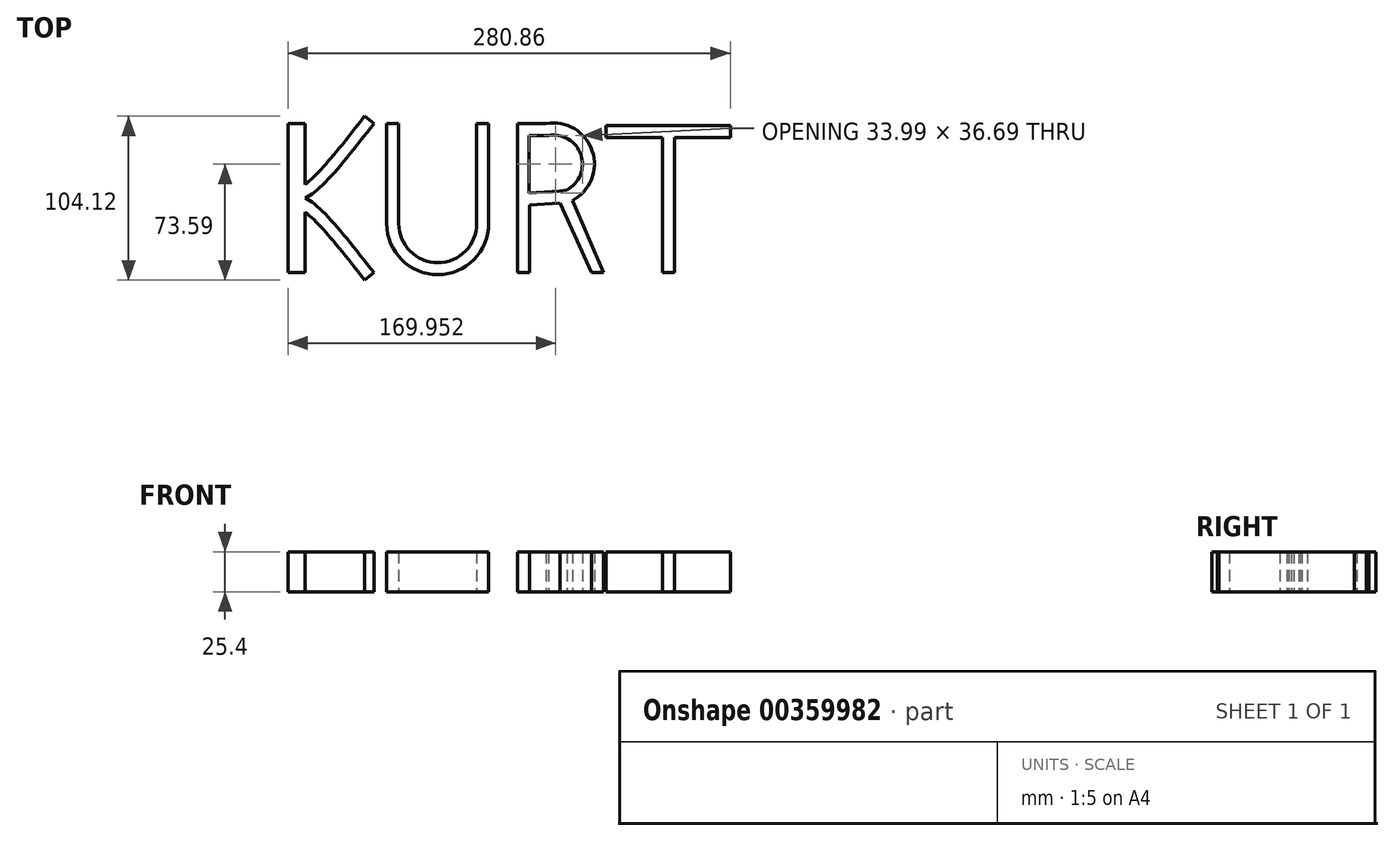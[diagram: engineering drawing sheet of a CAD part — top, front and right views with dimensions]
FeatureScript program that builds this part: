
annotation { "Feature Type Name" : "Feature", "Feature Type Description" : "" }
export const myFeature = defineFeature(function(context is Context, id is Id, definition is map)
    precondition{}
    {
        {
            var Q0;
            Q0=qCreatedBy(makeId("Top.planeOp"),FACE);
            var sketch = newSketch(context, id + "F0", { "sketchPlane" : qUnion([Q0])});
            skLineSegment(sketch, "E0.bottom", {"start": v(-95.51, 40.74) * mm, "end": v(-84.71, 40.74) * mm});
            skLineSegment(sketch, "E0.top", {"start": v(-95.51, -54.02) * mm, "end": v(-84.71, -54.02) * mm});
            skLineSegment(sketch, "E0.left", {"start": v(-95.51, 40.74) * mm, "end": v(-95.51, -54.02) * mm});
            skLineSegment(sketch, "E0.right", {"start": v(-84.71, 40.74) * mm, "end": v(-84.71, -54.02) * mm});
            skFitSpline(sketch, "E1", {"points": [v(-95.51, -6.64) * mm, v(-84.71, -6.64) * mm, v(-41.01, 40.74) * mm], "startDerivative": vector(33.65, -9.7) * mm, "endDerivative": vector(70.25, 90.47) * mm});
            skFitSpline(sketch, "E2", {"points": [v(-95.51, -6.64) * mm, v(-84.71, -6.64) * mm, v(-41.01, -54.02) * mm], "startDerivative": vector(33.65, 9.7) * mm, "endDerivative": vector(70.25, -90.47) * mm});
            skFitSpline(sketch, "E3.0", {"points": [v(-93.4, 0.68) * mm, v(-92.7, 0.48) * mm, v(-91.5, 0.14) * mm, v(-90.45, -0.06) * mm, v(-89.82, -0.1) * mm, v(-89.41, -0.1) * mm, v(-89.01, -0.06) * mm, v(-88.56, 0.04) * mm, v(-88.08, 0.2) * mm, v(-87.63, 0.4) * mm, v(-87.23, 0.6) * mm, v(-86.77, 0.84) * mm, v(-86.1, 1.25) * mm, v(-84.75, 2.14) * mm, v(-82.47, 3.92) * mm, v(-79.32, 6.78) * mm, v(-75.87, 10.27) * mm, v(-72.17, 14.3) * mm, v(-68.27, 18.78) * mm, v(-62.86, 25.27) * mm, v(-55.8, 34.13) * mm, v(-49.96, 41.65) * mm, v(-47.03, 45.42) * mm]});
            skFitSpline(sketch, "E4.0", {"points": [v(-93.4, -13.96) * mm, v(-92.7, -13.76) * mm, v(-91.5, -13.42) * mm, v(-90.45, -13.22) * mm, v(-89.82, -13.17) * mm, v(-89.41, -13.18) * mm, v(-89.01, -13.22) * mm, v(-88.56, -13.32) * mm, v(-88.08, -13.48) * mm, v(-87.63, -13.68) * mm, v(-87.23, -13.87) * mm, v(-86.77, -14.12) * mm, v(-86.1, -14.52) * mm, v(-84.75, -15.41) * mm, v(-82.47, -17.2) * mm, v(-79.32, -20.06) * mm, v(-75.87, -23.54) * mm, v(-72.17, -27.57) * mm, v(-68.27, -32.06) * mm, v(-62.86, -38.55) * mm, v(-55.8, -47.41) * mm, v(-49.96, -54.93) * mm, v(-47.03, -58.7) * mm]});
            skLineSegment(sketch, "E5", {"start": v(-47.03, 45.42) * mm, "end": v(-41.01, 40.74) * mm});
            skLineSegment(sketch, "E6", {"start": v(-47.03, -58.7) * mm, "end": v(-41.01, -54.02) * mm});
            skLineSegment(sketch, "E7", {"start": v(-25.26, 40.74) * mm, "end": v(-25.26, -22.76) * mm});
            skLineSegment(sketch, "E8", {"start": v(24.34, 40.74) * mm, "end": v(24.34, -22.76) * mm});
            skArc(sketch, "E9", {"start": v(-25.26, -22.76) * mm, "mid": v(-0.46, -47.55) * mm, "end": v(24.34, -22.76) * mm});
            skLineSegment(sketch, "E10.0", {"start": v(31.96, 40.74) * mm, "end": v(31.96, -22.76) * mm});
            skArc(sketch, "E10.1", {"start": v(-32.88, -22.76) * mm, "mid": v(-0.46, -55.17) * mm, "end": v(31.96, -22.76) * mm});
            skLineSegment(sketch, "E10.2", {"start": v(-32.88, 40.74) * mm, "end": v(-32.88, -22.76) * mm});
            skLineSegment(sketch, "E11", {"start": v(-32.88, 40.74) * mm, "end": v(-25.26, 40.74) * mm});
            skLineSegment(sketch, "E12", {"start": v(24.34, 40.74) * mm, "end": v(31.96, 40.74) * mm});
            skLineSegment(sketch, "E13", {"start": v(50.32, 40.74) * mm, "end": v(50.32, -54.02) * mm});
            skPoint(sketch, "E13.endSnap0", {"position": v(-90.11, -54.02) * mm});
            skLineSegment(sketch, "E14", {"start": v(50.32, -54.02) * mm, "end": v(57.93, -54.02) * mm});
            skLineSegment(sketch, "E15", {"start": v(57.93, -54.02) * mm, "end": v(57.93, -11.06) * mm});
            skLineSegment(sketch, "E16", {"start": v(50.32, 40.74) * mm, "end": v(68.49, 40.74) * mm});
            skArc(sketch, "E17", {"start": v(68.49, 40.74) * mm, "mid": v(97.68, 23.35) * mm, "end": v(85.06, -8.2) * mm});
            skLineSegment(sketch, "E18", {"start": v(85.06, -8.2) * mm, "end": v(104.82, -54.02) * mm});
            skLineSegment(sketch, "E19", {"start": v(104.82, -54.02) * mm, "end": v(97.2, -54.02) * mm});
            skLineSegment(sketch, "E20", {"start": v(97.2, -54.02) * mm, "end": v(77.33, -9.83) * mm});
            skLineSegment(sketch, "E21", {"start": v(57.93, -11.06) * mm, "end": v(77.33, -9.83) * mm});
            skArc(sketch, "E22.0", {"start": v(69.77, 33.23) * mm, "mid": v(90.46, 20.91) * mm, "end": v(81.52, -1.45) * mm});
            skLineSegment(sketch, "E23.0", {"start": v(57.45, -3.45) * mm, "end": v(76.84, -2.23) * mm});
            skLineSegment(sketch, "E24", {"start": v(76.84, -2.23) * mm, "end": v(81.52, -1.45) * mm});
            skLineSegment(sketch, "E25", {"start": v(57.45, -3.45) * mm, "end": v(57.45, 33.23) * mm});
            skLineSegment(sketch, "E26", {"start": v(57.45, 33.23) * mm, "end": v(69.77, 33.23) * mm});
            skLineSegment(sketch, "E27.bottom", {"start": v(106.54, 39.53) * mm, "end": v(185.35, 39.53) * mm});
            skLineSegment(sketch, "E27.top", {"start": v(106.54, 31.9) * mm, "end": v(185.35, 31.9) * mm});
            skLineSegment(sketch, "E27.left", {"start": v(106.54, 39.53) * mm, "end": v(106.54, 31.9) * mm});
            skLineSegment(sketch, "E27.right", {"start": v(185.35, 39.53) * mm, "end": v(185.35, 31.9) * mm});
            skPoint(sketch, "E28.endSnap0", {"position": v(101.01, -54.02) * mm});
            skLineSegment(sketch, "E29.bottom", {"start": v(145.95, 31.9) * mm, "end": v(142.14, 31.9) * mm});
            skLineSegment(sketch, "E29.top", {"start": v(145.95, -54.02) * mm, "end": v(142.14, -54.02) * mm});
            skLineSegment(sketch, "E29.right", {"start": v(142.14, 31.9) * mm, "end": v(142.14, -54.02) * mm});
            skLineSegment(sketch, "E30.MirrorCS", {"start": v(149.76, 31.9) * mm, "end": v(149.76, -54.02) * mm});
            skLineSegment(sketch, "E31.MirrorCS", {"start": v(145.95, -54.02) * mm, "end": v(149.76, -54.02) * mm});
            skPoint(sketch, "E28.end.orphan", {"position": v(145.95, -54.02) * mm});
            skSolve(sketch);
        }
        {
            var Q0;
            Q0=qSketchRegion(id+"F0",true);
            extrude(context, id + "F1", {"entities" : qUnion([Q0]), "depth" : 25.4 * mm});
        }
    });
